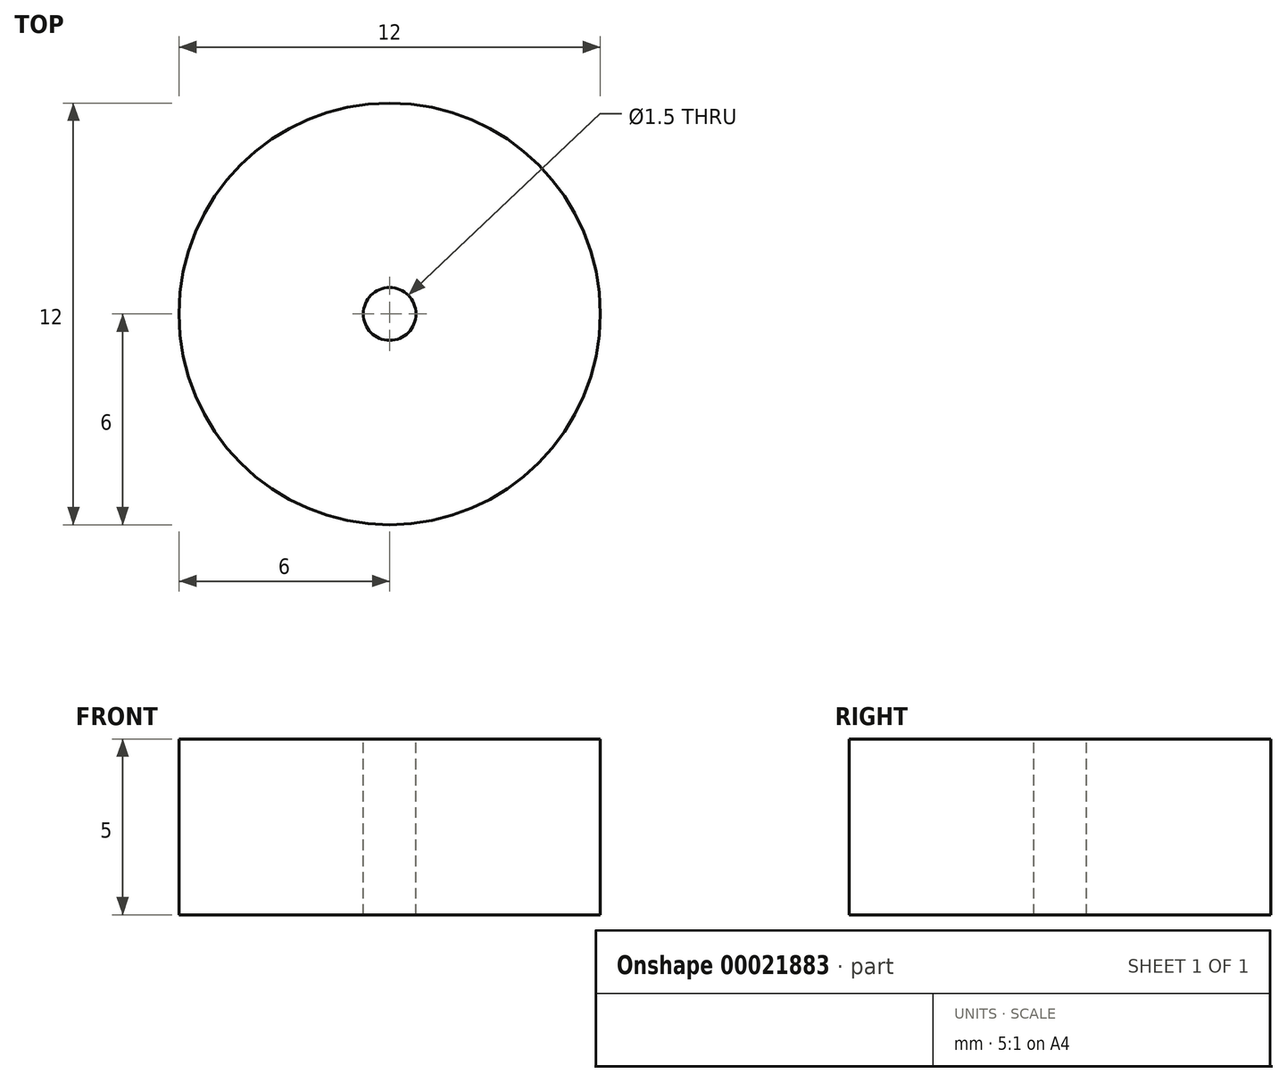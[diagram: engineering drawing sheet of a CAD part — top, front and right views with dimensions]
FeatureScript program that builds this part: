
annotation { "Feature Type Name" : "Feature", "Feature Type Description" : "" }
export const myFeature = defineFeature(function(context is Context, id is Id, definition is map)
    precondition{}
    {
        {
            var Q0;
            Q0=qCreatedBy(makeId("Top.planeOp"),FACE);
            var sketch = newSketch(context, id + "F0", { "sketchPlane" : qUnion([Q0])});
            skCircle(sketch, "E0", {"center": v(0, 0) * mm, "radius": 6 * mm});
            skSolve(sketch);
        }
        {
            var Q0;
            Q0 = qSketchRegion(id + "F0", true);
            extrude(context, id + "F1", {"entities" : qUnion([Q0]), "depth" : 5 * mm});
        }
        {
            var Q0;
            Q0=makeQuery(id+"F1.opExtrude","CAP_FACE",FACE,{"disambiguationData":[OSD([sQuery(id+"F0.wireOp",EDGE,"E0")])],"isStart":false});
            var sketch = newSketch(context, id + "F2", { "sketchPlane" : qUnion([Q0])});
            skPoint(sketch, "E1", {"position": v(0, 0) * mm});
            skSolve(sketch);
        }
        {
            var Q0;
            Q0=sQuery(id+"F2.wireOp",VERTEX,"E1");
            var Q1;
            Q1=makeQuery(id+"F1.opExtrude","SWEPT_BODY",BODY,{"disambiguationData":[OSD([sQuery(id+"F0.wireOp",EDGE,"E0")])]});
            hole(context, id + "F3", {"style" : HoleStyle.SIMPLE, "holeDiameter" : 1.5 * mm, "endStyle" : HoleEndStyle.THROUGH, "locations" : qUnion([Q0]), "scope" : qUnion([Q1])});
        }
    });
